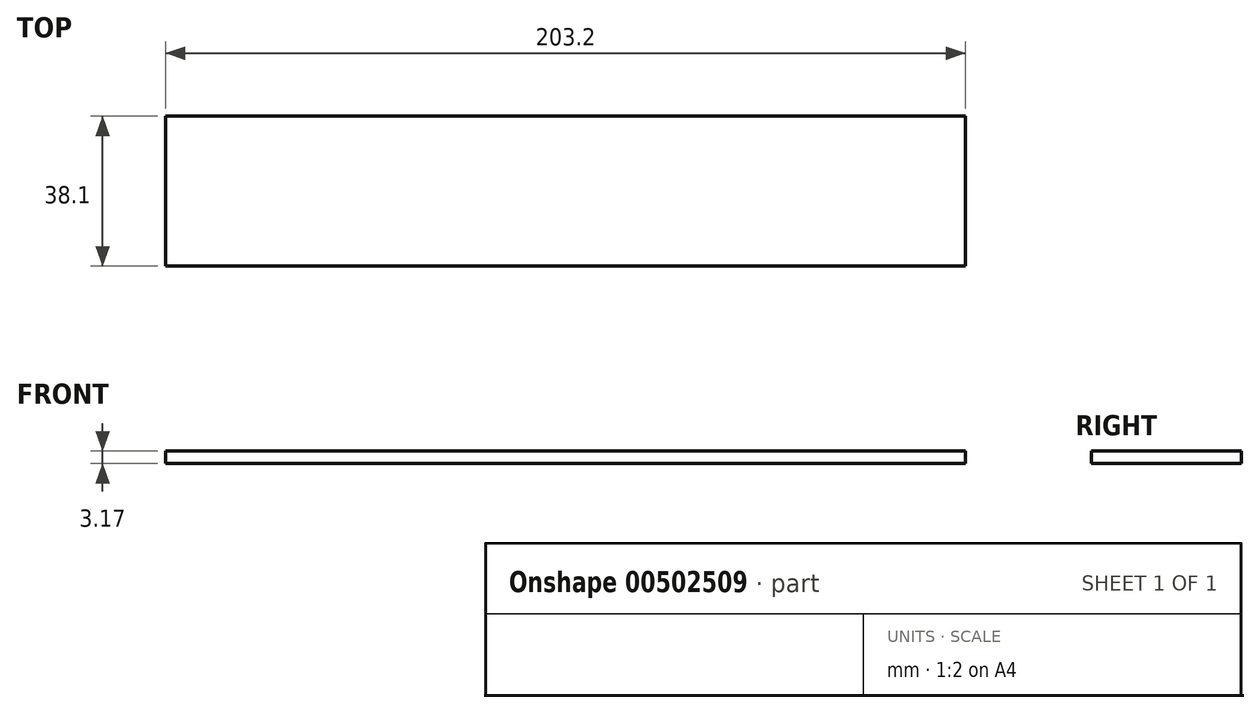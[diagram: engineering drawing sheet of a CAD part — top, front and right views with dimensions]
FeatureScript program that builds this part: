
annotation { "Feature Type Name" : "Feature", "Feature Type Description" : "" }
export const myFeature = defineFeature(function(context is Context, id is Id, definition is map)
    precondition{}
    {
        {
            var Q0;
            Q0=qCreatedBy(makeId("Top.planeOp"),FACE);
            var sketch = newSketch(context, id + "F0", { "sketchPlane" : qUnion([Q0])});
            skLineSegment(sketch, "E0", {"start": v(0, 0) * mm, "end": v(203.2, 0) * mm});
            skLineSegment(sketch, "E1", {"start": v(203.2, 0) * mm, "end": v(203.2, -38.1) * mm});
            skLineSegment(sketch, "E2", {"start": v(203.2, -38.1) * mm, "end": v(0, -38.1) * mm});
            skLineSegment(sketch, "E3", {"start": v(0, -38.1) * mm, "end": v(0, 0) * mm});
            skSolve(sketch);
        }
        {
            var Q0;
            Q0=qSketchRegion(id+"F0",true);
            extrude(context, id + "F1", {"entities" : qUnion([Q0]), "depth" : 3.17 * mm});
        }
    });
